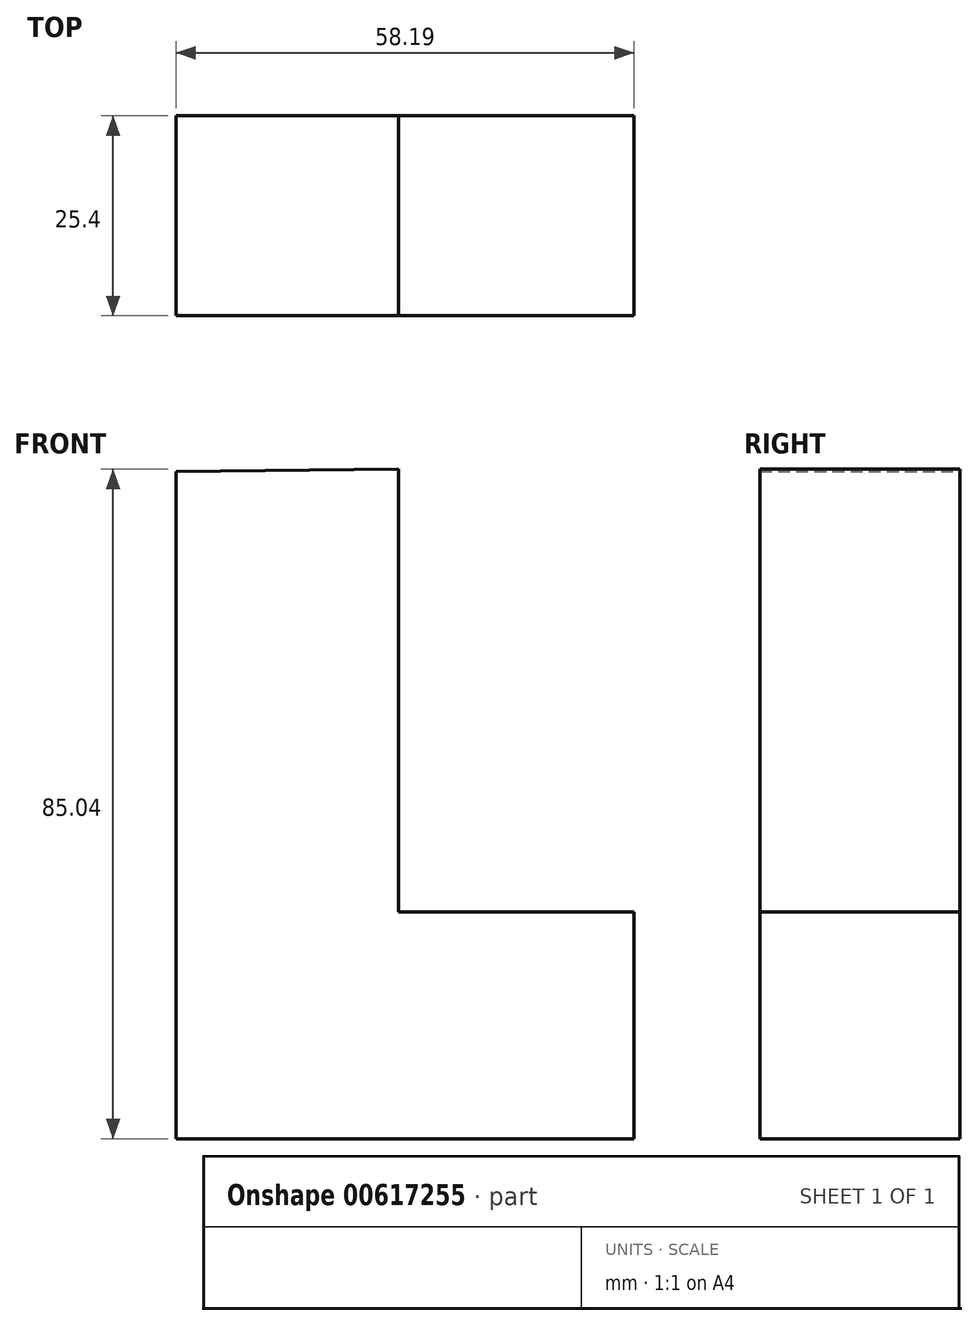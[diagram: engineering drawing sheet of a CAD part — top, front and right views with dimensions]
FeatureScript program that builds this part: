
annotation { "Feature Type Name" : "Feature", "Feature Type Description" : "" }
export const myFeature = defineFeature(function(context is Context, id is Id, definition is map)
    precondition{}
    {
        {
            var Q0;
            Q0=qCreatedBy(makeId("Front.planeOp"),FACE);
            var sketch = newSketch(context, id + "F0", { "sketchPlane" : qUnion([Q0])});
            skLineSegment(sketch, "E0", {"start": v(-37.07, 53.85) * mm, "end": v(-37.07, -30.91) * mm});
            skLineSegment(sketch, "E1", {"start": v(-37.07, -30.91) * mm, "end": v(21.12, -30.91) * mm});
            skLineSegment(sketch, "E2", {"start": v(21.12, -30.91) * mm, "end": v(21.12, -2.1) * mm});
            skLineSegment(sketch, "E3", {"start": v(21.12, -2.1) * mm, "end": v(-8.81, -2.1) * mm});
            skLineSegment(sketch, "E4", {"start": v(-8.81, -2.1) * mm, "end": v(-8.81, 54.13) * mm});
            skLineSegment(sketch, "E5", {"start": v(-37.07, 53.85) * mm, "end": v(-8.81, 54.13) * mm});
            skSolve(sketch);
        }
        {
            var Q0;
            Q0 = qSketchRegion(id + "F0", true);
            extrude(context, id + "F1", {"entities" : qUnion([Q0]), "depth" : 25.4 * mm, "offsetDistance" : 25.4 * mm});
        }
    });
